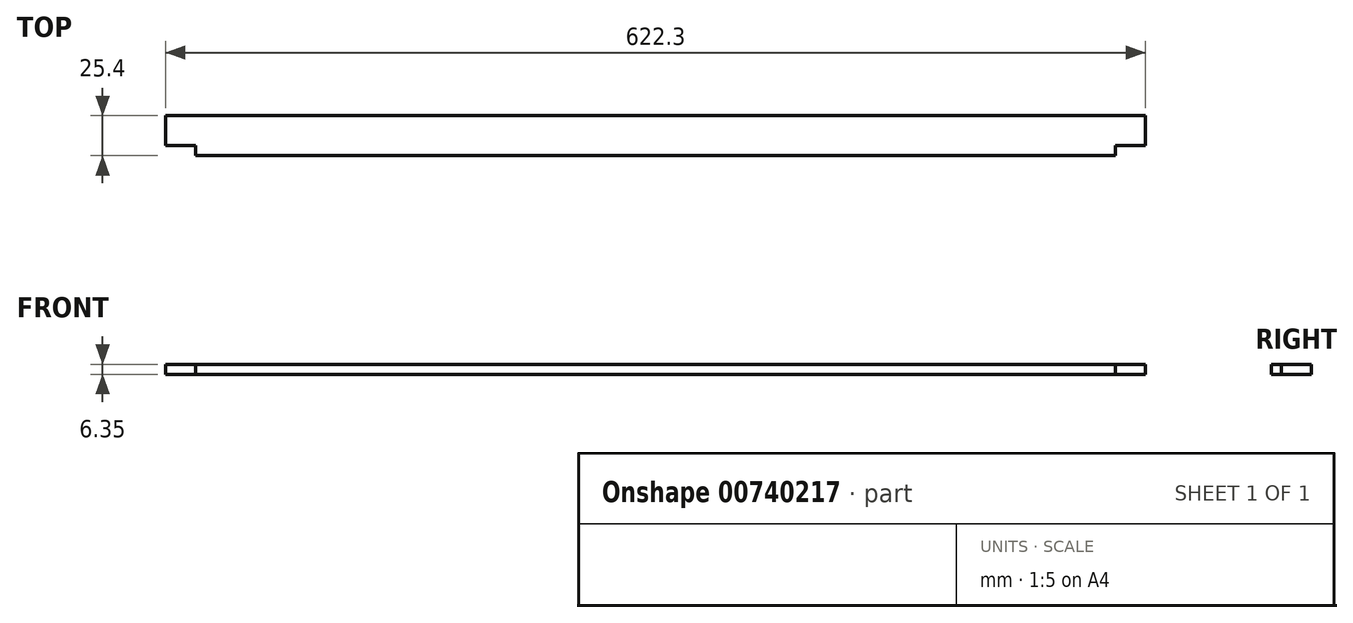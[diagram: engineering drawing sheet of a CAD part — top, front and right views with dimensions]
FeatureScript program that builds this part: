
annotation { "Feature Type Name" : "Feature", "Feature Type Description" : "" }
export const myFeature = defineFeature(function(context is Context, id is Id, definition is map)
    precondition{}
    {
        {
            var Q0;
            Q0=qCreatedBy(makeId("Top.planeOp"),FACE);
            var sketch = newSketch(context, id + "F0", { "sketchPlane" : qUnion([Q0])});
            skLineSegment(sketch, "E0.bottom", {"start": v(0, 0) * mm, "end": v(622.3, 0) * mm});
            skLineSegment(sketch, "E0.top", {"start": v(0, -25.4) * mm, "end": v(622.3, -25.4) * mm});
            skLineSegment(sketch, "E0.left", {"start": v(0, 0) * mm, "end": v(0, -25.4) * mm});
            skLineSegment(sketch, "E0.right", {"start": v(622.3, 0) * mm, "end": v(622.3, -25.4) * mm});
            skLineSegment(sketch, "E1.bottom", {"start": v(0, -25.4) * mm, "end": v(19.05, -25.4) * mm});
            skLineSegment(sketch, "E1.top", {"start": v(0, -19.05) * mm, "end": v(19.05, -19.05) * mm});
            skLineSegment(sketch, "E1.left", {"start": v(0, -25.4) * mm, "end": v(0, -19.05) * mm});
            skLineSegment(sketch, "E1.right", {"start": v(19.05, -25.4) * mm, "end": v(19.05, -19.05) * mm});
            skLineSegment(sketch, "E2.bottom", {"start": v(622.3, -25.4) * mm, "end": v(603.25, -25.4) * mm});
            skLineSegment(sketch, "E2.top", {"start": v(622.3, -19.05) * mm, "end": v(603.25, -19.05) * mm});
            skLineSegment(sketch, "E2.left", {"start": v(622.3, -25.4) * mm, "end": v(622.3, -19.05) * mm});
            skLineSegment(sketch, "E2.right", {"start": v(603.25, -25.4) * mm, "end": v(603.25, -19.05) * mm});
            skSolve(sketch);
        }
        {
            var Q0;
            Q0=makeQuery(id+"F0.imprint","IMPRINT",FACE,{"disambiguationData":[TD([[makeQuery(id+"F0.imprint","IMPRINT",EDGE,{"derivedFrom":sQuery(id+"F0.wireOp",EDGE,"E0.bottom")}),-1.0]])]});
            extrude(context, id + "F1", {"entities" : qUnion([Q0]), "depth" : 6.35 * mm, "offsetDistance" : 25.4 * mm});
        }
    });
